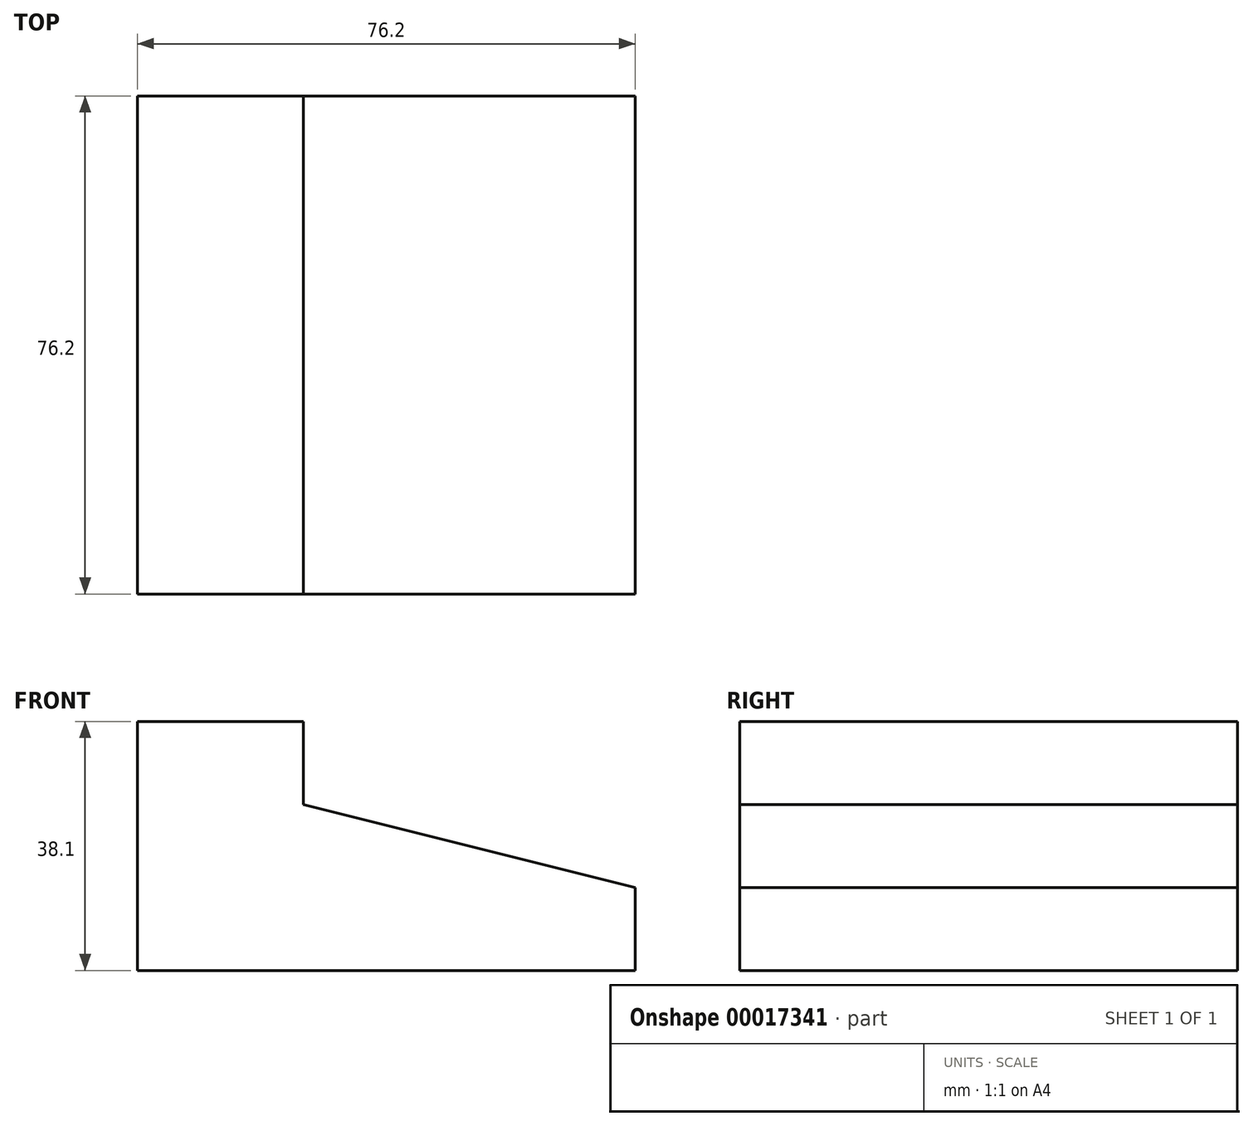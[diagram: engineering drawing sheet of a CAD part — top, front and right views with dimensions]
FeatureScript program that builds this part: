
annotation { "Feature Type Name" : "Feature", "Feature Type Description" : "" }
export const myFeature = defineFeature(function(context is Context, id is Id, definition is map)
    precondition{}
    {
        {
            var Q0;
            Q0=qCreatedBy(makeId("Front.planeOp"),FACE);
            var sketch = newSketch(context, id + "F0", { "sketchPlane" : qUnion([Q0])});
            skLineSegment(sketch, "E0", {"start": v(-25.4, 15.43) * mm, "end": v(-25.4, -22.67) * mm});
            skLineSegment(sketch, "E1", {"start": v(-25.4, -22.67) * mm, "end": v(50.8, -22.67) * mm});
            skLineSegment(sketch, "E2", {"start": v(0, 2.73) * mm, "end": v(0, 15.43) * mm});
            skLineSegment(sketch, "E3", {"start": v(0, 15.43) * mm, "end": v(-25.4, 15.43) * mm});
            skLineSegment(sketch, "E4", {"start": v(50.8, -9.97) * mm, "end": v(0, 2.73) * mm});
            skLineSegment(sketch, "E5", {"start": v(50.8, -9.97) * mm, "end": v(50.8, -22.67) * mm});
            skSolve(sketch);
        }
        {
            var Q0;
            Q0=makeQuery(id+"F0.imprint","IMPRINT",FACE,{"disambiguationData":[TD([[makeQuery(id+"F0.imprint","IMPRINT",EDGE,{"derivedFrom":sQuery(id+"F0.wireOp",EDGE,"E0")}),1.0]])]});
            extrude(context, id + "F1", {"entities" : qUnion([Q0]), "depth" : 76.2 * mm});
        }
    });
